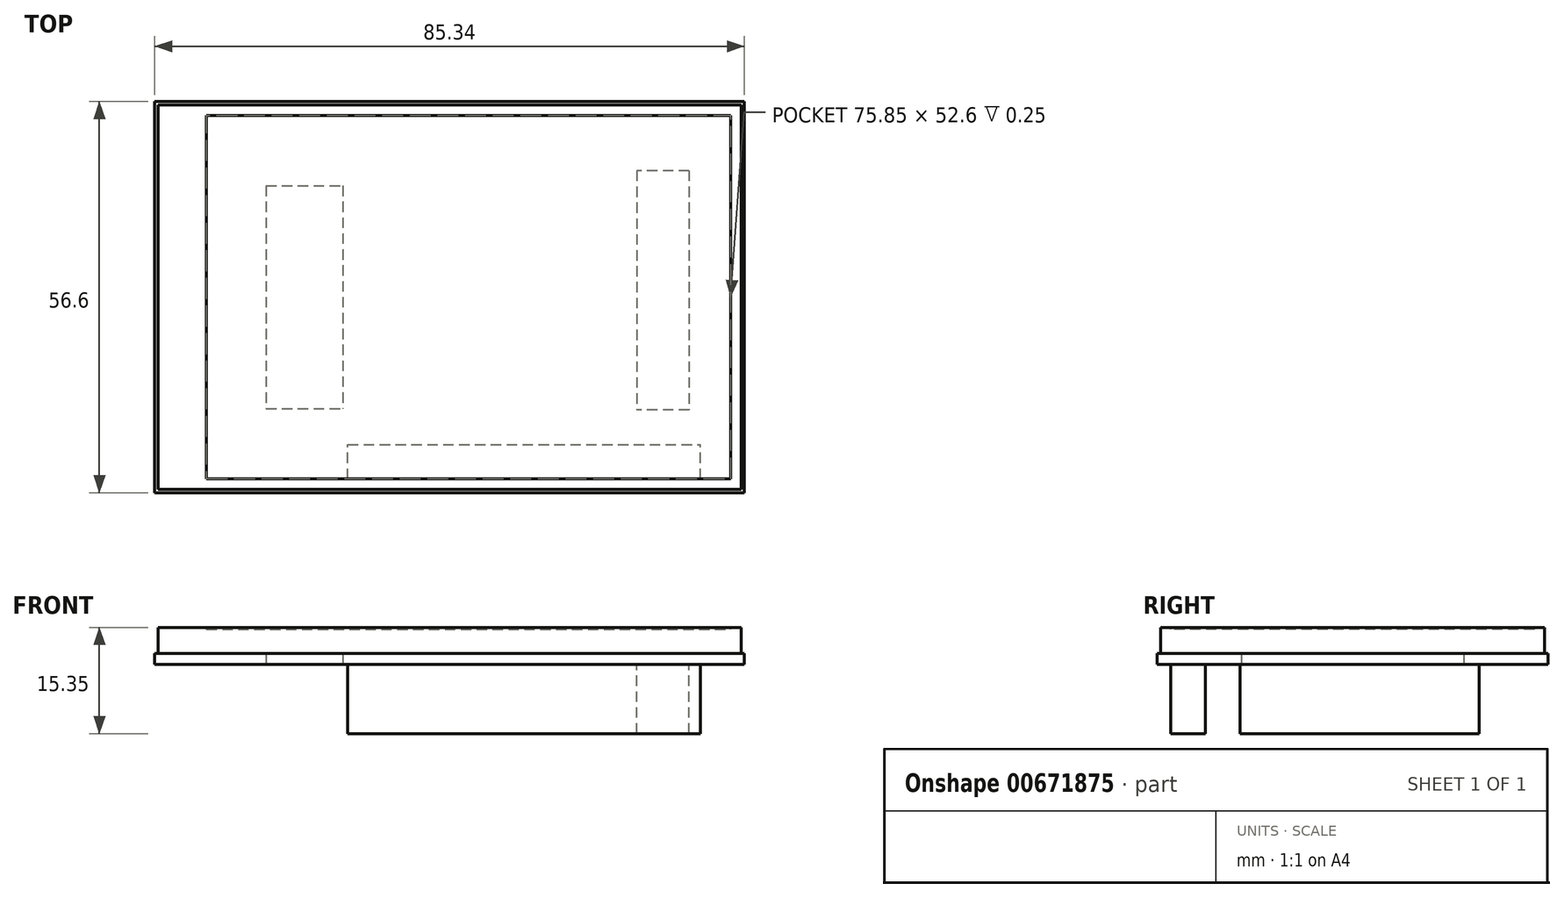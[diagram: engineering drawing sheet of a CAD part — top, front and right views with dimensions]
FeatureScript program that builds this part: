
annotation { "Feature Type Name" : "Feature", "Feature Type Description" : "" }
export const myFeature = defineFeature(function(context is Context, id is Id, definition is map)
    precondition{}
    {
        {
            var Q0;
            Q0=qCreatedBy(makeId("Top.planeOp"),FACE);
            var sketch = newSketch(context, id + "F0", { "sketchPlane" : qUnion([Q0])});
            skLineSegment(sketch, "E0.bottom", {"start": v(42.67, 28.3) * mm, "end": v(-42.67, 28.3) * mm});
            skLineSegment(sketch, "E0.top", {"start": v(42.67, -28.3) * mm, "end": v(-42.67, -28.3) * mm});
            skLineSegment(sketch, "E0.left", {"start": v(42.67, 28.3) * mm, "end": v(42.67, -28.3) * mm});
            skLineSegment(sketch, "E0.right", {"start": v(-42.67, 28.3) * mm, "end": v(-42.67, -28.3) * mm});
            skPoint(sketch, "E0.middle", {"position": v(0, 0) * mm});
            skLineSegment(sketch, "E1.bottom", {"start": v(-26.56, 16.13) * mm, "end": v(-15.45, 16.13) * mm});
            skLineSegment(sketch, "E1.top", {"start": v(-26.57, -16.12) * mm, "end": v(-15.46, -16.12) * mm});
            skLineSegment(sketch, "E1.left", {"start": v(-26.56, 16.13) * mm, "end": v(-26.56, -16.12) * mm});
            skLineSegment(sketch, "E1.right", {"start": v(-15.45, 16.13) * mm, "end": v(-15.46, -16.12) * mm});
            skPoint(sketch, "E1.middle", {"position": v(-21, 0) * mm});
            skSolve(sketch);
        }
        {
            var Q0;
            Q0=makeQuery(id+"F0.imprint","IMPRINT",FACE,{"disambiguationData":[TD([[makeQuery(id+"F0.imprint","IMPRINT",EDGE,{"derivedFrom":sQuery(id+"F0.wireOp",EDGE,"E0.bottom")}),1.0]])]});
            extrude(context, id + "F1", {"entities" : qUnion([Q0]), "depth" : 1.6 * mm, "offsetDistance" : 25 * mm});
        }
        {
            var Q0;
            Q0=makeQuery(id+"F1.opExtrude","CAP_FACE",FACE,{"disambiguationData":[OSD([sQuery(id+"F0.wireOp",EDGE,"E0.bottom"),sQuery(id+"F0.wireOp",EDGE,"E0.top"),sQuery(id+"F0.wireOp",EDGE,"E0.left"),sQuery(id+"F0.wireOp",EDGE,"E0.right"),sQuery(id+"F0.wireOp",EDGE,"E1.bottom"),sQuery(id+"F0.wireOp",EDGE,"E1.top"),sQuery(id+"F0.wireOp",EDGE,"E1.left"),sQuery(id+"F0.wireOp",EDGE,"E1.right")])],"isStart":false});
            var sketch = newSketch(context, id + "F2", { "sketchPlane" : qUnion([Q0])});
            skLineSegment(sketch, "E2.bottom", {"start": v(-42.17, 27.8) * mm, "end": v(42.17, 27.8) * mm});
            skLineSegment(sketch, "E2.top", {"start": v(-42.17, -27.8) * mm, "end": v(42.17, -27.8) * mm});
            skLineSegment(sketch, "E2.left", {"start": v(-42.17, 27.8) * mm, "end": v(-42.17, -27.8) * mm});
            skLineSegment(sketch, "E2.right", {"start": v(42.17, 27.8) * mm, "end": v(42.17, -27.8) * mm});
            skPoint(sketch, "E2.middle", {"position": v(0, 0) * mm});
            skSolve(sketch);
        }
        {
            var Q0;
            Q0 = qSketchRegion(id + "F2", true);
            extrude(context, id + "F3", {"entities" : qUnion([Q0]), "operationType" : NewBodyOperationType.ADD, "depth" : 3.75 * mm, "offsetDistance" : 25 * mm});
        }
        {
            var Q0;
            Q0=makeQuery(id+"F3.opExtrude","CAP_FACE",FACE,{"disambiguationData":[OSD([sQuery(id+"F2.wireOp",EDGE,"E2.bottom"),sQuery(id+"F2.wireOp",EDGE,"E2.top"),sQuery(id+"F2.wireOp",EDGE,"E2.left"),sQuery(id+"F2.wireOp",EDGE,"E2.right")])],"isStart":false});
            var sketch = newSketch(context, id + "F4", { "sketchPlane" : qUnion([Q0])});
            skLineSegment(sketch, "E3.bottom", {"start": v(-35.17, 26.3) * mm, "end": v(40.67, 26.3) * mm});
            skLineSegment(sketch, "E3.top", {"start": v(-35.17, -26.3) * mm, "end": v(40.67, -26.3) * mm});
            skLineSegment(sketch, "E3.left", {"start": v(-35.17, 26.3) * mm, "end": v(-35.17, -26.3) * mm});
            skLineSegment(sketch, "E3.right", {"start": v(40.68, 26.3) * mm, "end": v(40.67, -26.3) * mm});
            skPoint(sketch, "E3.middle", {"position": v(2.75, 0) * mm});
            skSolve(sketch);
        }
        {
            var Q0;
            Q0=makeQuery(id+"F4.imprint","IMPRINT",FACE,{"disambiguationData":[TD([[makeQuery(id+"F4.imprint","IMPRINT",EDGE,{"derivedFrom":sQuery(id+"F4.wireOp",EDGE,"E3.bottom")}),-1.0]])]});
            extrude(context, id + "F5", {"entities" : qUnion([Q0]), "operationType" : NewBodyOperationType.REMOVE, "oppositeDirection" : true, "depth" : 0.25 * mm, "offsetDistance" : 25 * mm});
        }
        {
            var Q0;
            Q0=makeQuery(id+"F1.opExtrude","CAP_FACE",FACE,{"disambiguationData":[OSD([sQuery(id+"F0.wireOp",EDGE,"E0.bottom"),sQuery(id+"F0.wireOp",EDGE,"E0.top"),sQuery(id+"F0.wireOp",EDGE,"E0.left"),sQuery(id+"F0.wireOp",EDGE,"E0.right"),sQuery(id+"F0.wireOp",EDGE,"E1.bottom"),sQuery(id+"F0.wireOp",EDGE,"E1.top"),sQuery(id+"F0.wireOp",EDGE,"E1.left"),sQuery(id+"F0.wireOp",EDGE,"E1.right")])],"isStart":true});
            var sketch = newSketch(context, id + "F6", { "sketchPlane" : qUnion([Q0])});
            skLineSegment(sketch, "E4.bottom", {"start": v(-14.73, 26.3) * mm, "end": v(36.27, 26.3) * mm});
            skLineSegment(sketch, "E4.top", {"start": v(-14.73, 21.3) * mm, "end": v(36.27, 21.3) * mm});
            skLineSegment(sketch, "E4.left", {"start": v(-14.73, 26.3) * mm, "end": v(-14.73, 21.3) * mm});
            skLineSegment(sketch, "E4.right", {"start": v(36.27, 26.3) * mm, "end": v(36.27, 21.3) * mm});
            skPoint(sketch, "E4.middle", {"position": v(10.77, 23.8) * mm});
            skLineSegment(sketch, "E5.bottom", {"start": v(34.67, -18.3) * mm, "end": v(27.07, -18.3) * mm});
            skLineSegment(sketch, "E5.top", {"start": v(34.67, 16.3) * mm, "end": v(27.07, 16.3) * mm});
            skLineSegment(sketch, "E5.left", {"start": v(34.67, -18.3) * mm, "end": v(34.67, 16.3) * mm});
            skLineSegment(sketch, "E5.right", {"start": v(27.07, -18.3) * mm, "end": v(27.07, 16.3) * mm});
            skPoint(sketch, "E5.middle", {"position": v(30.87, -1) * mm});
            skSolve(sketch);
        }
        {
            var Q0;
            Q0=makeQuery(id+"F6.imprint","IMPRINT",FACE,{"disambiguationData":[TD([[makeQuery(id+"F6.imprint","IMPRINT",EDGE,{"derivedFrom":sQuery(id+"F6.wireOp",EDGE,"E5.bottom")}),-1.0]])]});
            var Q1;
            Q1=makeQuery(id+"F6.imprint","IMPRINT",FACE,{"disambiguationData":[TD([[makeQuery(id+"F6.imprint","IMPRINT",EDGE,{"derivedFrom":sQuery(id+"F6.wireOp",EDGE,"E4.bottom")}),-1.0]])]});
            extrude(context, id + "F7", {"entities" : qUnion([Q0, Q1]), "operationType" : NewBodyOperationType.ADD, "depth" : 10 * mm, "offsetDistance" : 25 * mm});
        }
    });
